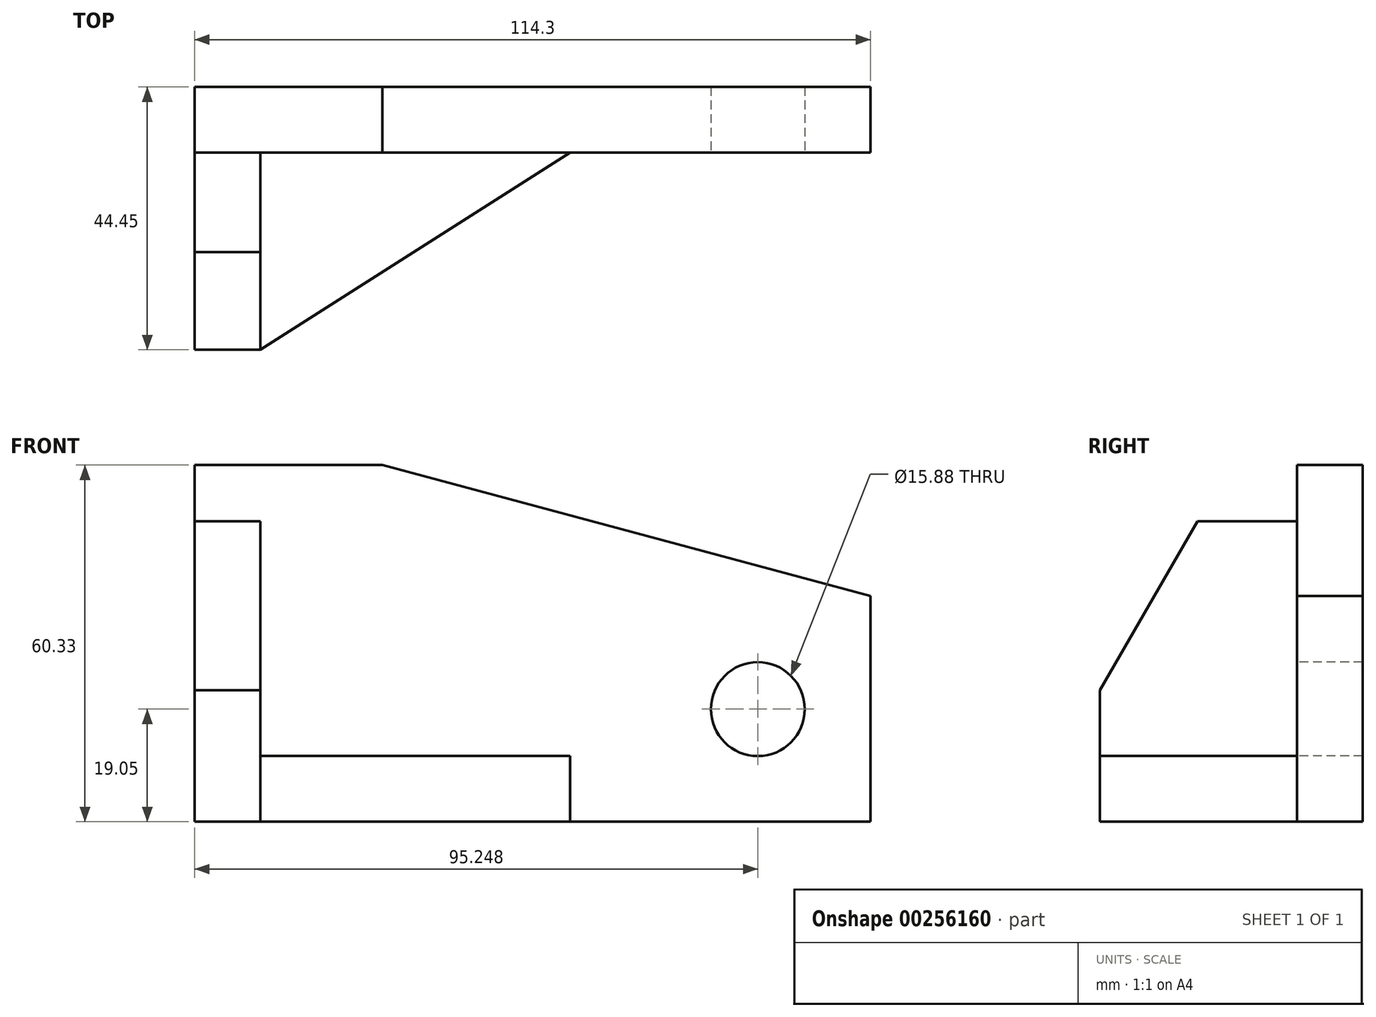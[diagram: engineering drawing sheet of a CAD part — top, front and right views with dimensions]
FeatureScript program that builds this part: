
annotation { "Feature Type Name" : "Feature", "Feature Type Description" : "" }
export const myFeature = defineFeature(function(context is Context, id is Id, definition is map)
    precondition{}
    {
        {
            var Q0;
            Q0=qCreatedBy(makeId("Top.planeOp"),FACE);
            var sketch = newSketch(context, id + "F0", { "sketchPlane" : qUnion([Q0])});
            skLineSegment(sketch, "E0.bottom", {"start": v(0, 0) * mm, "end": v(52.39, 0) * mm});
            skLineSegment(sketch, "E0.left", {"start": v(0, 0) * mm, "end": v(0, -33.34) * mm});
            skLineSegment(sketch, "E1", {"start": v(0, -33.34) * mm, "end": v(52.39, 0) * mm});
            skSolve(sketch);
        }
        {
            var Q0;
            Q0=qCreatedBy(makeId("Right.planeOp"),FACE);
            var sketch = newSketch(context, id + "F1", { "sketchPlane" : qUnion([Q0])});
            skLineSegment(sketch, "E2.bottom", {"start": v(0, 0) * mm, "end": v(-33.34, 0) * mm});
            skLineSegment(sketch, "E2.top", {"start": v(0, 50.8) * mm, "end": v(-16.84, 50.8) * mm});
            skLineSegment(sketch, "E2.left", {"start": v(0, 0) * mm, "end": v(0, 50.8) * mm});
            skLineSegment(sketch, "E2.right", {"start": v(-33.34, 0) * mm, "end": v(-33.34, 22.22) * mm});
            skLineSegment(sketch, "E3", {"start": v(-33.34, 22.22) * mm, "end": v(-16.84, 50.8) * mm});
            skSolve(sketch);
        }
        {
            var Q0;
            Q0=qCreatedBy(makeId("Front.planeOp"),FACE);
            var sketch = newSketch(context, id + "F2", { "sketchPlane" : qUnion([Q0])});
            skLineSegment(sketch, "E4.bottom", {"start": v(-11.11, 60.33) * mm, "end": v(20.64, 60.33) * mm});
            skLineSegment(sketch, "E4.top", {"start": v(-11.11, 0) * mm, "end": v(103.19, 0) * mm});
            skLineSegment(sketch, "E4.left", {"start": v(-11.11, 60.33) * mm, "end": v(-11.11, 0) * mm});
            skLineSegment(sketch, "E4.right", {"start": v(103.19, 38.2) * mm, "end": v(103.19, 0) * mm});
            skLineSegment(sketch, "E5", {"start": v(20.64, 60.33) * mm, "end": v(103.19, 38.2) * mm});
            skPoint(sketch, "E6.orphan", {"position": v(103.19, 60.33) * mm});
            skCircle(sketch, "E7", {"center": v(84.14, 19.05) * mm, "radius": 7.94 * mm});
            skSolve(sketch);
        }
        {
            var Q0;
            Q0=makeQuery(id+"F0.imprint","IMPRINT",FACE,{"disambiguationData":[TD([[makeQuery(id+"F0.imprint","IMPRINT",EDGE,{"derivedFrom":sQuery(id+"F0.wireOp",EDGE,"E0.bottom")}),-1.0]])]});
            extrude(context, id + "F3", {"entities" : qUnion([Q0]), "depth" : 11.1 * mm});
        }
        {
            var Q0;
            Q0=makeQuery(id+"F1.imprint","IMPRINT",FACE,{"disambiguationData":[TD([[makeQuery(id+"F1.imprint","IMPRINT",EDGE,{"derivedFrom":sQuery(id+"F1.wireOp",EDGE,"E2.bottom")}),-1.0]])]});
            extrude(context, id + "F4", {"entities" : qUnion([Q0]), "operationType" : NewBodyOperationType.ADD, "oppositeDirection" : true, "depth" : 11.1 * mm});
        }
        {
            var Q0;
            Q0=makeQuery(id+"F2.imprint","IMPRINT",FACE,{"disambiguationData":[TD([[makeQuery(id+"F2.imprint","IMPRINT",EDGE,{"derivedFrom":sQuery(id+"F2.wireOp",EDGE,"E4.top")}),1.0]])]});
            extrude(context, id + "F5", {"entities" : qUnion([Q0]), "oppositeDirection" : true, "depth" : 11.1 * mm});
        }
    });
